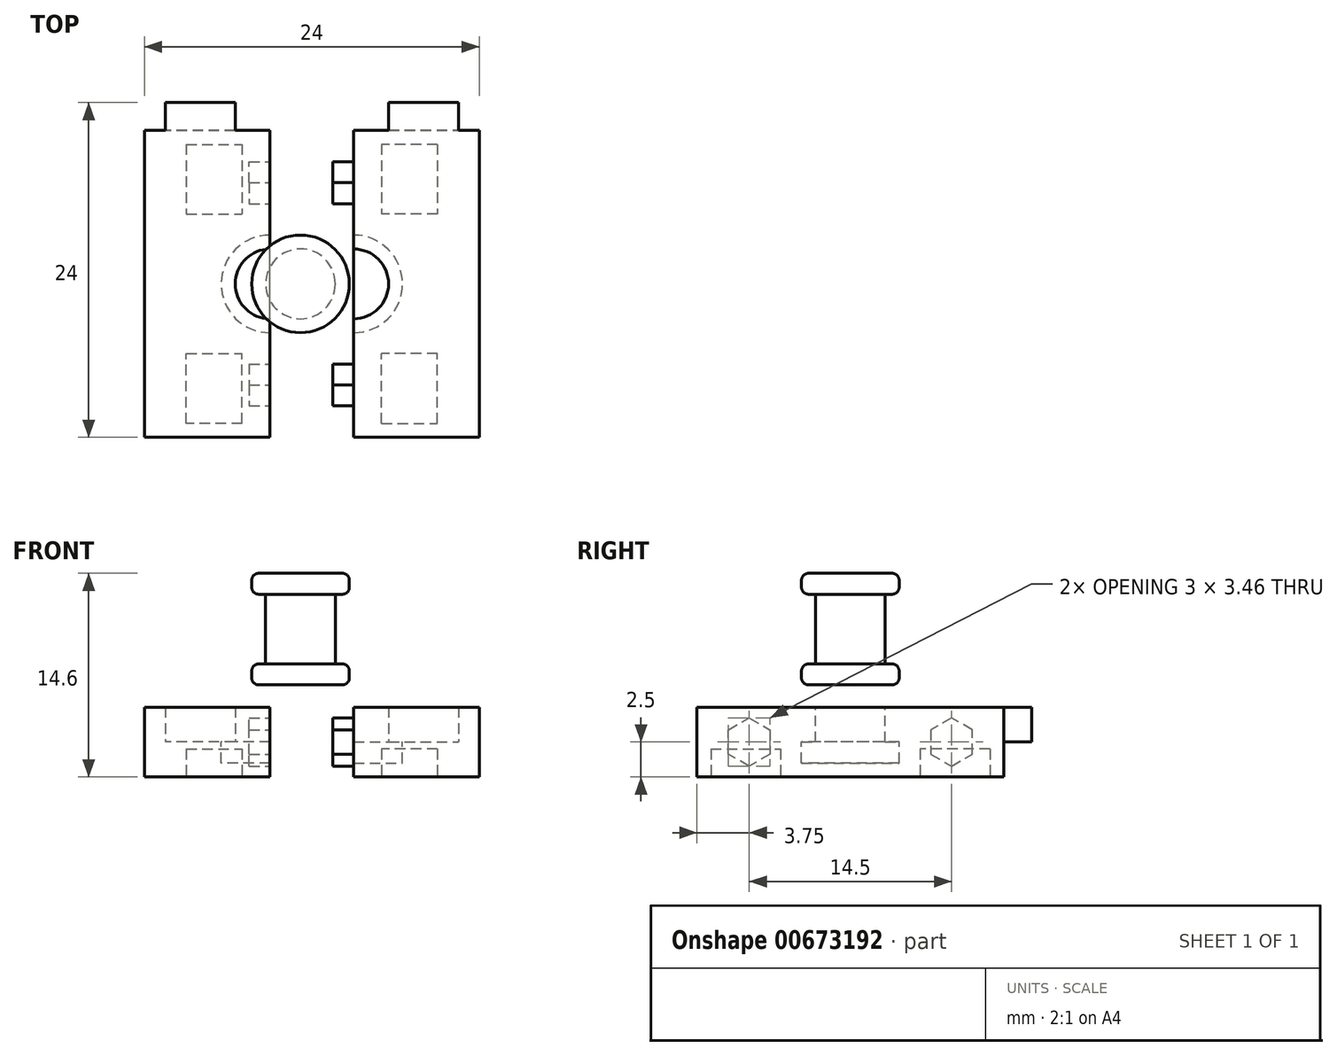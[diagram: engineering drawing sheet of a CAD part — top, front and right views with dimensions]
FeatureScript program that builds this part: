
annotation { "Feature Type Name" : "Feature", "Feature Type Description" : "" }
export const myFeature = defineFeature(function(context is Context, id is Id, definition is map)
    precondition{}
    {
        {
            var Q0;
            Q0=qCreatedBy(makeId("Top.planeOp"),FACE);
            var sketch = newSketch(context, id + "F0", { "sketchPlane" : qUnion([Q0])});
            skLineSegment(sketch, "E0.bottom", {"start": v(3, 20) * mm, "end": v(7, 20) * mm});
            skLineSegment(sketch, "E0.top", {"start": v(3, 15) * mm, "end": v(7, 15) * mm});
            skLineSegment(sketch, "E0.left", {"start": v(3, 20) * mm, "end": v(3, 15) * mm});
            skLineSegment(sketch, "E0.right", {"start": v(7, 20) * mm, "end": v(7, 15) * mm});
            skLineSegment(sketch, "E1.MirrorCS", {"start": v(7, 0) * mm, "end": v(7, 5) * mm});
            skLineSegment(sketch, "E2.MirrorCS", {"start": v(3, 5) * mm, "end": v(7, 5) * mm});
            skLineSegment(sketch, "E3.MirrorCS", {"start": v(3, 0) * mm, "end": v(3, 5) * mm});
            skLineSegment(sketch, "E4", {"start": v(0, 0) * mm, "end": v(0, -1) * mm, "construction": true});
            skLineSegment(sketch, "E5.bottom", {"start": v(0, -1) * mm, "end": v(9, -1) * mm});
            skLineSegment(sketch, "E5.top", {"start": v(0, 21) * mm, "end": v(9, 21) * mm});
            skLineSegment(sketch, "E5.right", {"start": v(9, -1) * mm, "end": v(9, 21) * mm});
            skLineSegment(sketch, "E6", {"start": v(7, 0) * mm, "end": v(3, 0) * mm});
            skLineSegment(sketch, "E7", {"start": v(0, -1) * mm, "end": v(0, 21) * mm});
            skSolve(sketch);
        }
        {
            var Q0;
            Q0=makeQuery(id+"F0.imprint","IMPRINT",FACE,{"disambiguationData":[TD([[makeQuery(id+"F0.imprint","IMPRINT",EDGE,{"derivedFrom":sQuery(id+"F0.wireOp",EDGE,"E0.bottom")}),1.0]])]});
            var Q1;
            Q1=makeQuery(id+"F0.imprint","IMPRINT",FACE,{"disambiguationData":[TD([[makeQuery(id+"F0.imprint","IMPRINT",EDGE,{"derivedFrom":sQuery(id+"F0.wireOp",EDGE,"E0.bottom")}),-1.0]])]});
            var Q2;
            Q2=makeQuery(id+"F0.imprint","IMPRINT",FACE,{"disambiguationData":[TD([[makeQuery(id+"F0.imprint","IMPRINT",EDGE,{"derivedFrom":sQuery(id+"F0.wireOp",EDGE,"E1.MirrorCS")}),1.0]])]});
            extrude(context, id + "F1", {"entities" : qUnion([Q0, Q1, Q2]), "depth" : 5 * mm});
        }
        {
            var Q0;
            Q0=makeQuery(id+"F0.imprint","IMPRINT",FACE,{"disambiguationData":[TD([[makeQuery(id+"F0.imprint","IMPRINT",EDGE,{"derivedFrom":sQuery(id+"F0.wireOp",EDGE,"E1.MirrorCS")}),1.0]])]});
            var Q1;
            Q1=makeQuery(id+"F0.imprint","IMPRINT",FACE,{"disambiguationData":[TD([[makeQuery(id+"F0.imprint","IMPRINT",EDGE,{"derivedFrom":sQuery(id+"F0.wireOp",EDGE,"E0.bottom")}),-1.0]])]});
            extrude(context, id + "F2", {"entities" : qUnion([Q0, Q1]), "operationType" : NewBodyOperationType.REMOVE, "depth" : 2 * mm});
        }
        {
            var Q0;
            Q0=makeQuery(id+"F1.opExtrude","CAP_FACE",FACE,{"disambiguationData":[OSD([sQuery(id+"F0.wireOp",EDGE,"E5.bottom"),sQuery(id+"F0.wireOp",EDGE,"E5.top"),sQuery(id+"F0.wireOp",EDGE,"E5.left"),sQuery(id+"F0.wireOp",EDGE,"E5.right")])],"isStart":false});
            var sketch = newSketch(context, id + "F3", { "sketchPlane" : qUnion([Q0])});
            skArc(sketch, "E8", {"start": v(9, 13.5) * mm, "mid": v(5.5, 10) * mm, "end": v(9, 6.5) * mm});
            skArc(sketch, "E9", {"start": v(9, 12.5) * mm, "mid": v(6.5, 10) * mm, "end": v(9, 7.5) * mm});
            skLineSegment(sketch, "E10", {"start": v(9, 13.5) * mm, "end": v(9, 6.5) * mm});
            skSolve(sketch);
        }
        {
            var Q0;
            {var subQ0=sQuery(id+"F3.wireOp",EDGE,"E8");Q0=makeQuery(id+"F3.imprint","IMPRINT",FACE,{"disambiguationData":[TD([[makeQuery(id+"F3.imprint","IMPRINT",EDGE,{"derivedFrom":subQ0}),1.0]])]});}
            var Q1;
            {var subQ0=sQuery(id+"F3.wireOp",EDGE,"E9");Q1=makeQuery(id+"F3.imprint","IMPRINT",FACE,{"disambiguationData":[TD([[makeQuery(id+"F3.imprint","IMPRINT",EDGE,{"derivedFrom":subQ0}),1.0]])]});}
            extrude(context, id + "F4", {"entities" : qUnion([Q0, Q1]), "operationType" : NewBodyOperationType.REMOVE, "oppositeDirection" : true, "depth" : 4 * mm});
        }
        {
            var Q0;
            {var subQ0=sQuery(id+"F3.wireOp",EDGE,"E8");Q0=makeQuery(id+"F3.imprint","IMPRINT",FACE,{"disambiguationData":[TD([[makeQuery(id+"F3.imprint","IMPRINT",EDGE,{"derivedFrom":subQ0}),1.0]])]});}
            extrude(context, id + "F5", {"entities" : qUnion([Q0]), "operationType" : NewBodyOperationType.ADD, "oppositeDirection" : true, "depth" : 2.5 * mm});
        }
        {
            var Q0;
            {var subQ0=sQuery(id+"F3.wireOp",EDGE,"E10");var subQ2=sQuery(id+"F0.wireOp",EDGE,"E5.right");var subQ4=sQuery(id+"F3.wireOp",EDGE,"E9");Q0=makeQuery(id+"F5.boolean.opBoolean","MERGE",FACE,{"derivedFrom":[makeQuery(id+"F1.opExtrude","SWEPT_FACE",FACE,{"disambiguationData":[OSD([subQ2])]}),makeQuery(id+"F5.opExtrude","SWEPT_FACE",FACE,{"disambiguationData":[OSD([subQ0]),TDD([makeQuery(id+"F3.imprint","IMPRINT",EDGE,{"disambiguationData":[TD([[makeQuery(id+"F3.imprint","INTERSECT",VERTEX,{"disambiguationData":[OD(1.0)],"derivedFrom":[subQ4,subQ0]}),1.0]])],"derivedFrom":subQ0})])]}),makeQuery(id+"F5.opExtrude","SWEPT_FACE",FACE,{"disambiguationData":[OSD([subQ0]),TDD([makeQuery(id+"F3.imprint","IMPRINT",EDGE,{"disambiguationData":[TD([[makeQuery(id+"F3.imprint","INTERSECT",VERTEX,{"disambiguationData":[OD(0.0)],"derivedFrom":[subQ4,subQ0]}),-1.0]])],"derivedFrom":subQ0})])]})]});}
            var sketch = newSketch(context, id + "F6", { "sketchPlane" : qUnion([Q0])});
            skLineSegment(sketch, "E11", {"start": v(6.5, 0) * mm, "end": v(-1, 5) * mm, "construction": true});
            skLineSegment(sketch, "E12", {"start": v(-1, 0) * mm, "end": v(6.5, 5) * mm, "construction": true});
            skLineSegment(sketch, "E13", {"start": v(10, 1) * mm, "end": v(10, -2.42) * mm, "construction": true});
            skCircle(sketch, "E14.cCircle", {"center": v(2.75, 2.5) * mm, "radius": 1.5 * mm, "construction": true});
            skLineSegment(sketch, "E14.0", {"start": v(1.25, 1.63) * mm, "end": v(1.25, 3.37) * mm});
            skLineSegment(sketch, "E14.1", {"start": v(1.25, 3.37) * mm, "end": v(2.75, 4.23) * mm});
            skLineSegment(sketch, "E14.2", {"start": v(2.75, 4.23) * mm, "end": v(4.25, 3.37) * mm});
            skLineSegment(sketch, "E14.3", {"start": v(4.25, 3.37) * mm, "end": v(4.25, 1.63) * mm});
            skLineSegment(sketch, "E14.4", {"start": v(4.25, 1.63) * mm, "end": v(2.75, 0.77) * mm});
            skLineSegment(sketch, "E14.5", {"start": v(2.75, 0.77) * mm, "end": v(1.25, 1.63) * mm});
            skPoint(sketch, "E14.0.midPoint", {"position": v(1.25, 2.5) * mm});
            skLineSegment(sketch, "E15.MirrorCS", {"start": v(18.75, 3.37) * mm, "end": v(17.25, 4.23) * mm});
            skLineSegment(sketch, "E16.MirrorCS", {"start": v(17.25, 0.77) * mm, "end": v(18.75, 1.63) * mm});
            skLineSegment(sketch, "E17.MirrorCS", {"start": v(15.75, 1.63) * mm, "end": v(17.25, 0.77) * mm});
            skLineSegment(sketch, "E18.MirrorCS", {"start": v(17.25, 4.23) * mm, "end": v(15.75, 3.37) * mm});
            skLineSegment(sketch, "E19.MirrorCS", {"start": v(13.5, 0) * mm, "end": v(21, 5) * mm, "construction": true});
            skLineSegment(sketch, "E20.MirrorCS", {"start": v(21, 0) * mm, "end": v(13.5, 5) * mm, "construction": true});
            skLineSegment(sketch, "E21.MirrorCS", {"start": v(18.75, 1.63) * mm, "end": v(18.75, 3.37) * mm});
            skCircle(sketch, "E22.MirrorC", {"center": v(17.25, 2.5) * mm, "radius": 1.5 * mm, "construction": true});
            skLineSegment(sketch, "E23.MirrorCS", {"start": v(15.75, 3.37) * mm, "end": v(15.75, 1.63) * mm});
            skPoint(sketch, "E24.MirrorP", {"position": v(18.75, 2.5) * mm});
            skSolve(sketch);
        }
        {
            var Q0;
            Q0=qSketchRegion(id+"F6",true);
            extrude(context, id + "F7", {"entities" : qUnion([Q0]), "operationType" : NewBodyOperationType.REMOVE, "oppositeDirection" : true, "depth" : 1.5 * mm});
        }
        {
            var Q0;
            Q0=makeQuery(id+"F1.opExtrude","SWEPT_FACE",FACE,{"disambiguationData":[OSD([sQuery(id+"F0.wireOp",EDGE,"E5.top")])]});
            var sketch = newSketch(context, id + "F8", { "sketchPlane" : qUnion([Q0])});
            skLineSegment(sketch, "E25.bottom", {"start": v(-9, 5) * mm, "end": v(0, 5) * mm, "construction": true});
            skLineSegment(sketch, "E25.top", {"start": v(-9, 0) * mm, "end": v(0, 0) * mm, "construction": true});
            skLineSegment(sketch, "E25.left", {"start": v(-9, 5) * mm, "end": v(-9, 0) * mm, "construction": true});
            skLineSegment(sketch, "E25.right", {"start": v(0, 5) * mm, "end": v(0, 0) * mm, "construction": true});
            skLineSegment(sketch, "E26", {"start": v(-9, 5) * mm, "end": v(-6.5, 5) * mm, "construction": true});
            skLineSegment(sketch, "E27.bottom", {"start": v(-6.5, 5) * mm, "end": v(-1.5, 5) * mm});
            skLineSegment(sketch, "E27.top", {"start": v(-6.5, 2.5) * mm, "end": v(-1.5, 2.5) * mm});
            skLineSegment(sketch, "E27.left", {"start": v(-6.5, 5) * mm, "end": v(-6.5, 2.5) * mm});
            skLineSegment(sketch, "E27.right", {"start": v(-1.5, 5) * mm, "end": v(-1.5, 2.5) * mm});
            skSolve(sketch);
        }
        {
            var Q0;
            Q0=qSketchRegion(id+"F8",true);
            extrude(context, id + "F9", {"entities" : qUnion([Q0]), "operationType" : NewBodyOperationType.ADD, "depth" : 2 * mm});
        }
        {
            var Q0;
            Q0=qCreatedBy(makeId("Front.planeOp"),FACE);
            cPlane(context, id + "F10", {"entities" : qUnion([Q0]), "cplaneType" : CPlaneType.OFFSET, "offset" : 10 * mm, "oppositeDirection" : true, "width" : 150 * mm, "height" : 150 * mm});
        }
        {
            var Q0;
            Q0=qCreatedBy(makeId("Right.planeOp"),FACE);
            cPlane(context, id + "F11", {"entities" : qUnion([Q0]), "cplaneType" : CPlaneType.OFFSET, "offset" : 12 * mm, "width" : 150 * mm, "height" : 150 * mm});
        }
        {
            var Q0;
            Q0=makeQuery(id+"F1.opExtrude","SWEPT_BODY",BODY,{"disambiguationData":[OSD([sQuery(id+"F0.wireOp",EDGE,"E5.bottom"),sQuery(id+"F0.wireOp",EDGE,"E5.top"),sQuery(id+"F0.wireOp",EDGE,"E5.left"),sQuery(id+"F0.wireOp",EDGE,"E5.right")])]});
            var Q1;
            Q1=qCreatedBy(id+"F11.planeOp",FACE);
            mirror(context, id + "F12", {"entities" : qUnion([Q0]), "mirrorPlane" : qUnion([Q1])});
        }
        {
            var Q0;
            Q0=makeQuery(id+"F12.opPattern","COPY",FACE,{"derivedFrom":makeQuery(id+"F7.boolean.opBoolean","COPY",FACE,{"derivedFrom":makeQuery(id+"F7.opExtrude","CAP_FACE",FACE,{"disambiguationData":[OSD([sQuery(id+"F6.wireOp",EDGE,"E14.0"),sQuery(id+"F6.wireOp",EDGE,"E14.1"),sQuery(id+"F6.wireOp",EDGE,"E14.2"),sQuery(id+"F6.wireOp",EDGE,"E14.3"),sQuery(id+"F6.wireOp",EDGE,"E14.4"),sQuery(id+"F6.wireOp",EDGE,"E14.5")])],"isStart":false})}),"instanceName":"1"});
            var Q1;
            Q1=makeQuery(id+"F12.opPattern","COPY",FACE,{"derivedFrom":makeQuery(id+"F7.boolean.opBoolean","COPY",FACE,{"derivedFrom":makeQuery(id+"F7.opExtrude","CAP_FACE",FACE,{"disambiguationData":[OSD([sQuery(id+"F6.wireOp",EDGE,"E15.MirrorCS"),sQuery(id+"F6.wireOp",EDGE,"E16.MirrorCS"),sQuery(id+"F6.wireOp",EDGE,"E17.MirrorCS"),sQuery(id+"F6.wireOp",EDGE,"E18.MirrorCS"),sQuery(id+"F6.wireOp",EDGE,"E21.MirrorCS"),sQuery(id+"F6.wireOp",EDGE,"E23.MirrorCS")])],"isStart":false})}),"instanceName":"1"});
            extrude(context, id + "F13", {"entities" : qUnion([Q0, Q1]), "operationType" : NewBodyOperationType.ADD, "depth" : 3 * mm});
        }
        {
            var Q0;
            Q0=qCreatedBy(id+"F10.planeOp",FACE);
            var sketch = newSketch(context, id + "F14", { "sketchPlane" : qUnion([Q0])});
            skLineSegment(sketch, "E28", {"start": v(0, 0) * mm, "end": v(11.19, 0) * mm, "construction": true});
            skLineSegment(sketch, "E29", {"start": v(11.19, 0) * mm, "end": v(11.19, 13.2) * mm, "construction": true});
            skLineSegment(sketch, "E30", {"start": v(11.19, 6.6) * mm, "end": v(7.69, 6.6) * mm});
            skLineSegment(sketch, "E31", {"start": v(7.69, 6.6) * mm, "end": v(7.69, 8.1) * mm});
            skLineSegment(sketch, "E32", {"start": v(7.69, 8.1) * mm, "end": v(8.69, 8.1) * mm});
            skLineSegment(sketch, "E33", {"start": v(8.69, 8.1) * mm, "end": v(8.69, 10.6) * mm});
            skLineSegment(sketch, "E34", {"start": v(8.69, 10.6) * mm, "end": v(11.19, 10.6) * mm, "construction": true});
            skLineSegment(sketch, "E35.MirrorCS", {"start": v(8.69, 13.1) * mm, "end": v(8.69, 10.6) * mm});
            skLineSegment(sketch, "E36.MirrorCS", {"start": v(7.69, 13.1) * mm, "end": v(8.69, 13.1) * mm});
            skLineSegment(sketch, "E37.MirrorCS", {"start": v(11.19, 14.6) * mm, "end": v(7.69, 14.6) * mm});
            skLineSegment(sketch, "E38.MirrorCS", {"start": v(7.69, 14.6) * mm, "end": v(7.69, 13.1) * mm});
            skLineSegment(sketch, "E39", {"start": v(11.19, 14.6) * mm, "end": v(11.19, 6.6) * mm});
            skSolve(sketch);
        }
        {
            var Q0;
            Q0=qSketchRegion(id+"F14",true);
            var Q1;
            Q1=sQuery(id+"F14.wireOp",EDGE,"E39");
            revolve(context, id + "F15", {"entities" : qUnion([Q0]), "axis" : qUnion([Q1]), "revolveType" : RevolveType.FULL});
        }
        {
            var Q0;
            Q0=makeQuery(id+"F15.opRevolve","SWEPT_FACE",FACE,{"disambiguationData":[OSD([sQuery(id+"F14.wireOp",EDGE,"E37.MirrorCS")])]});
            var Q1;
            Q1=makeQuery(id+"F15.opRevolve","SWEPT_EDGE",EDGE,{"disambiguationData":[OSD([sQuery(id+"F14.wireOp",EDGE,"E31"),sQuery(id+"F14.wireOp",EDGE,"E32")])]});
            var Q2;
            Q2=makeQuery(id+"F15.opRevolve","SWEPT_FACE",FACE,{"disambiguationData":[OSD([sQuery(id+"F14.wireOp",EDGE,"E38.MirrorCS")])]});
            var Q3;
            Q3=makeQuery(id+"F15.opRevolve","SWEPT_FACE",FACE,{"disambiguationData":[OSD([sQuery(id+"F14.wireOp",EDGE,"E31")])]});
            fillet(context, id + "F16", {"entities" : qUnion([Q0, Q1, Q2, Q3]), "radius" : .5 * mm, "tangentPropagation" : true, "allowEdgeOverflow" : false});
        }
    });
